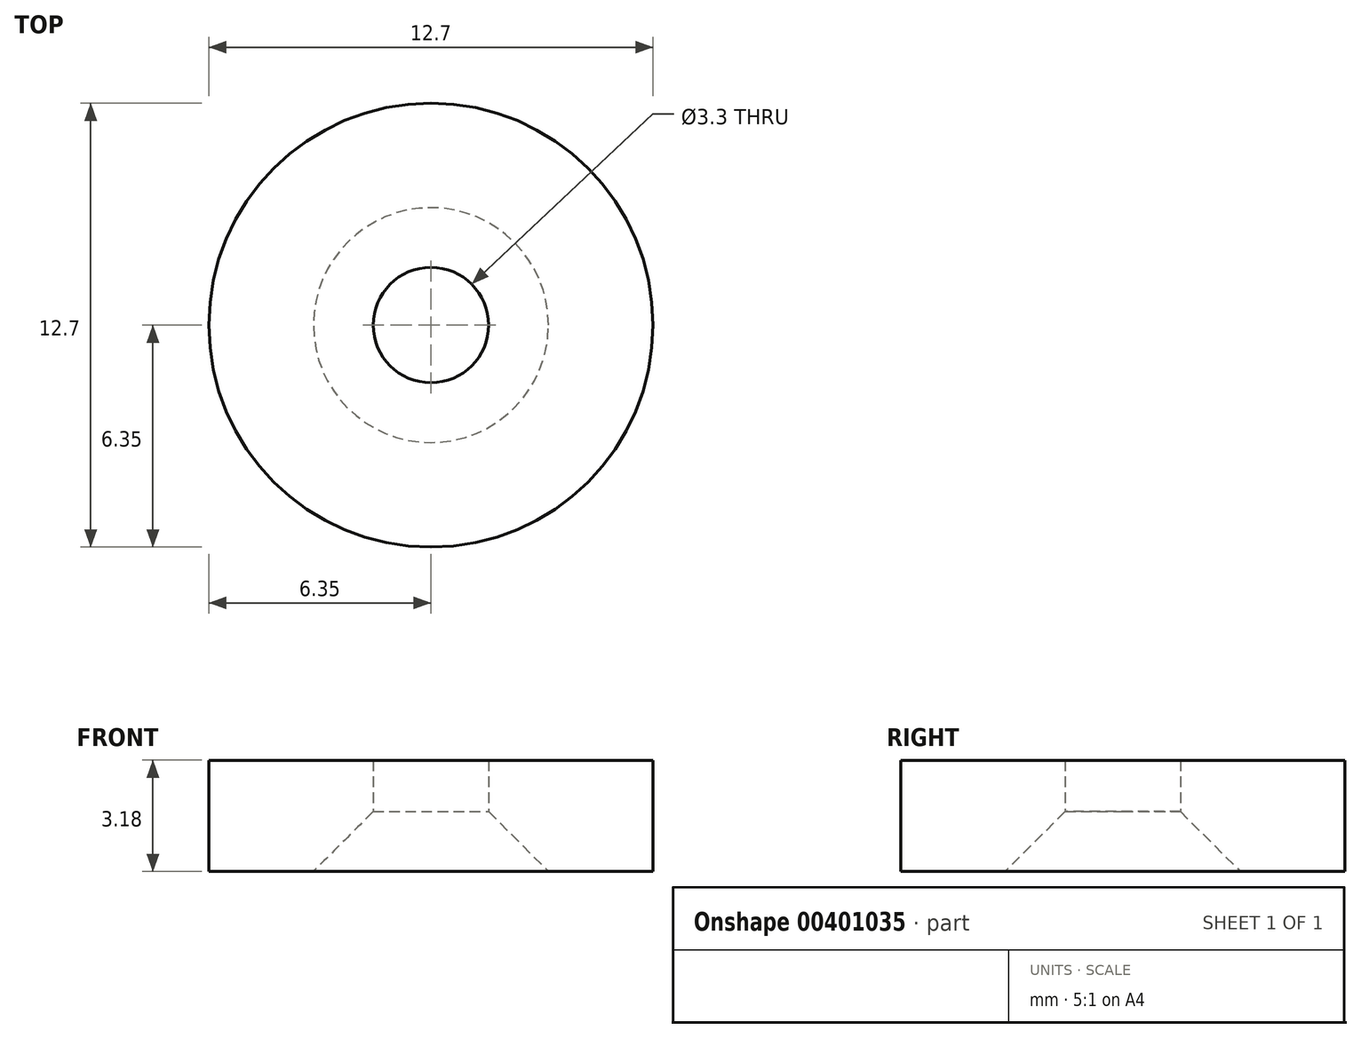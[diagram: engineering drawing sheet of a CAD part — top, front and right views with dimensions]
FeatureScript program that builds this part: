
annotation { "Feature Type Name" : "Feature", "Feature Type Description" : "" }
export const myFeature = defineFeature(function(context is Context, id is Id, definition is map)
    precondition{}
    {
        {
            var Q0;
            Q0=qCreatedBy(makeId("Top.planeOp"),FACE);
            var sketch = newSketch(context, id + "F0", { "sketchPlane" : qUnion([Q0])});
            skCircle(sketch, "E0", {"center": v(0, 0) * mm, "radius": 6.35 * mm});
            skSolve(sketch);
        }
        {
            var Q0;
            Q0=makeQuery(id+"F0.imprint","IMPRINT",FACE,{"disambiguationData":[TD([[makeQuery(id+"F0.imprint","IMPRINT",EDGE,{"derivedFrom":sQuery(id+"F0.wireOp",EDGE,"E0")}),1.0]])]});
            extrude(context, id + "F1", {"entities" : qUnion([Q0]), "depth" : 3.17 * mm});
        }
        {
            var Q0;
            Q0=sQuery(id+"F0.wireOp",VERTEX,"E0.center");
            var Q1;
            Q1=makeQuery(id+"F1.opExtrude","SWEPT_BODY",BODY,{"disambiguationData":[OSD([sQuery(id+"F0.wireOp",EDGE,"E0")])]});
            hole(context, id + "F2", {"style" : HoleStyle.C_SINK, "endStyle" : HoleEndStyle.THROUGH, "oppositeDirection" : true, "standardTappedOrClearance" : lookupTablePath({ "standard" : "ISO", "fit" : "Normal", "size" : "M3", "type" : "Clearance" }), "standardBlindInLast" : lookupTablePath({ "fit" : "Standard", "standard" : "ISO", "size" : "M3", "type" : "Clearance" }), "holeDiameter" : 3.3 * mm, "cSinkDiameter" : 6.72 * mm, "cSinkAngle" : 90 * degree, "isTappedThrough" : true, "tappedDepth" : 12.7 * mm, "tapClearance" : 3, "locations" : qUnion([Q0]), "scope" : qUnion([Q1])});
        }
    });
